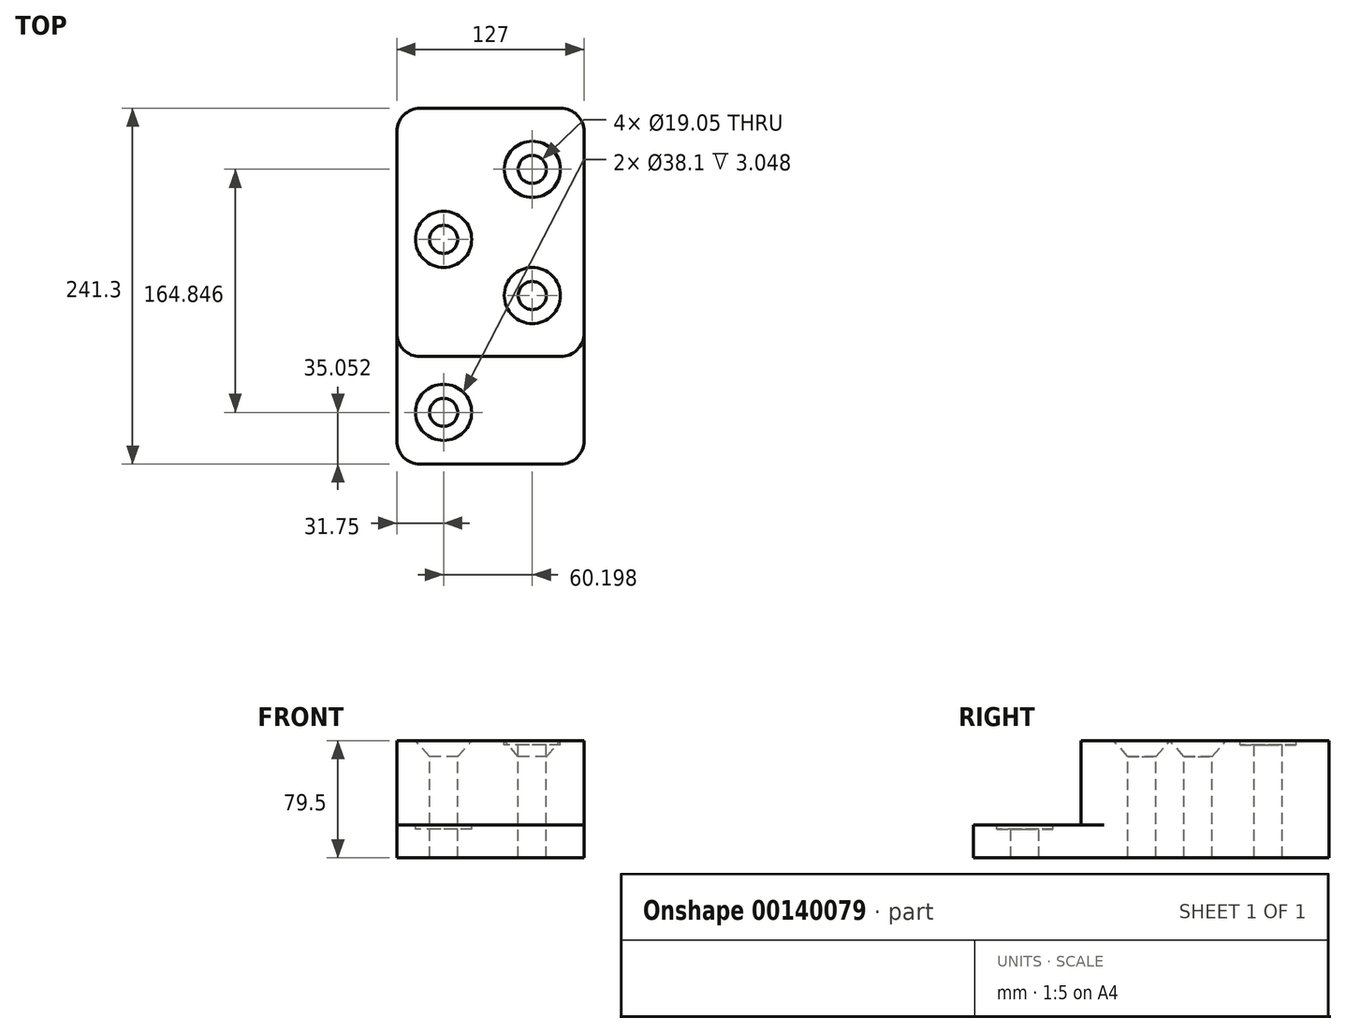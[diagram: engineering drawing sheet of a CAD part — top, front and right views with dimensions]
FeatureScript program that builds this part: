
annotation { "Feature Type Name" : "Feature", "Feature Type Description" : "" }
export const myFeature = defineFeature(function(context is Context, id is Id, definition is map)
    precondition{}
    {
        {
            var Q0;
            Q0=qCreatedBy(makeId("Right.planeOp"),FACE);
            var sketch = newSketch(context, id + "F0", { "sketchPlane" : qUnion([Q0])});
            skLineSegment(sketch, "E0", {"start": v(0, 0) * mm, "end": v(0, 22.35) * mm});
            skLineSegment(sketch, "E1", {"start": v(0, 22.35) * mm, "end": v(72.9, 22.35) * mm});
            skLineSegment(sketch, "E2", {"start": v(72.9, 22.35) * mm, "end": v(72.9, 79.5) * mm});
            skLineSegment(sketch, "E3", {"start": v(72.9, 79.5) * mm, "end": v(241.3, 79.5) * mm});
            skLineSegment(sketch, "E4", {"start": v(241.3, 79.5) * mm, "end": v(241.3, 0) * mm});
            skLineSegment(sketch, "E5", {"start": v(241.3, 0) * mm, "end": v(0, 0) * mm});
            skSolve(sketch);
        }
        {
            var Q0;
            Q0 = qSketchRegion(id + "F0", true);
            extrude(context, id + "F1", {"entities" : qUnion([Q0]), "depth" : 127 * mm});
        }
        {
            var Q0;
            Q0=makeQuery(id+"F1.opExtrude","CAP_EDGE",EDGE,{"disambiguationData":[OSD([sQuery(id+"F0.wireOp",EDGE,"E2")])],"isStart":false});
            var Q1;
            Q1=makeQuery(id+"F1.opExtrude","CAP_EDGE",EDGE,{"disambiguationData":[OSD([sQuery(id+"F0.wireOp",EDGE,"E2")])],"isStart":true});
            var Q2;
            Q2=makeQuery(id+"F1.opExtrude","CAP_EDGE",EDGE,{"disambiguationData":[OSD([sQuery(id+"F0.wireOp",EDGE,"E0")])],"isStart":false});
            var Q3;
            Q3=makeQuery(id+"F1.opExtrude","CAP_EDGE",EDGE,{"disambiguationData":[OSD([sQuery(id+"F0.wireOp",EDGE,"E0")])],"isStart":true});
            var Q4;
            Q4=makeQuery(id+"F1.opExtrude","CAP_EDGE",EDGE,{"disambiguationData":[OSD([sQuery(id+"F0.wireOp",EDGE,"E4")])],"isStart":false});
            var Q5;
            Q5=makeQuery(id+"F1.opExtrude","CAP_EDGE",EDGE,{"disambiguationData":[OSD([sQuery(id+"F0.wireOp",EDGE,"E4")])],"isStart":true});
            fillet(context, id + "F2", {"entities" : qUnion([Q0, Q1, Q2, Q3, Q4, Q5]), "radius" : 15.75 * mm, "tangentPropagation" : true, "allowEdgeOverflow" : false});
        }
        {
            var Q0;
            Q0=makeQuery(id+"F1.opExtrude","SWEPT_FACE",FACE,{"disambiguationData":[OSD([sQuery(id+"F0.wireOp",EDGE,"E3")])]});
            var sketch = newSketch(context, id + "F3", { "sketchPlane" : qUnion([Q0])});
            skPoint(sketch, "E6", {"position": v(91.95, 199.9) * mm});
            skPoint(sketch, "E7", {"position": v(31.75, 152.4) * mm});
            skPoint(sketch, "E8", {"position": v(91.95, 114.3) * mm});
            skPoint(sketch, "E9", {"position": v(31.75, 35.05) * mm});
            skSolve(sketch);
        }
        {
            var Q0;
            Q0=sQuery(id+"F3.wireOp",VERTEX,"E8");
            var Q1;
            Q1=sQuery(id+"F3.wireOp",VERTEX,"E7");
            var Q2;
            Q2=makeQuery(id+"F1.opExtrude","SWEPT_BODY",BODY,{"disambiguationData":[OSD([sQuery(id+"F0.wireOp",EDGE,"E0"),sQuery(id+"F0.wireOp",EDGE,"E1"),sQuery(id+"F0.wireOp",EDGE,"E2"),sQuery(id+"F0.wireOp",EDGE,"E3"),sQuery(id+"F0.wireOp",EDGE,"E4"),sQuery(id+"F0.wireOp",EDGE,"E5")])]});
            hole(context, id + "F4", {"style" : HoleStyle.C_SINK, "endStyle" : HoleEndStyle.THROUGH, "holeDiameter" : 19.05 * mm, "cSinkDiameter" : 38.1 * mm, "cSinkAngle" : 82 * degree, "locations" : qUnion([Q0, Q1]), "scope" : qUnion([Q2]), "isTappedThrough" : true});
        }
        {
            var Q0;
            Q0=sQuery(id+"F3.wireOp",VERTEX,"E6");
            var Q1;
            Q1=sQuery(id+"F3.wireOp",VERTEX,"E9");
            var Q2;
            Q2=makeQuery(id+"F1.opExtrude","SWEPT_BODY",BODY,{"disambiguationData":[OSD([sQuery(id+"F0.wireOp",EDGE,"E0"),sQuery(id+"F0.wireOp",EDGE,"E1"),sQuery(id+"F0.wireOp",EDGE,"E2"),sQuery(id+"F0.wireOp",EDGE,"E3"),sQuery(id+"F0.wireOp",EDGE,"E4"),sQuery(id+"F0.wireOp",EDGE,"E5")])]});
            hole(context, id + "F5", {"style" : HoleStyle.C_BORE, "endStyle" : HoleEndStyle.THROUGH, "holeDiameter" : 19.05 * mm, "cBoreDiameter" : 38.1 * mm, "cBoreDepth" : 3.05 * mm, "locations" : qUnion([Q0, Q1]), "scope" : qUnion([Q2]), "isTappedThrough" : true});
        }
    });
